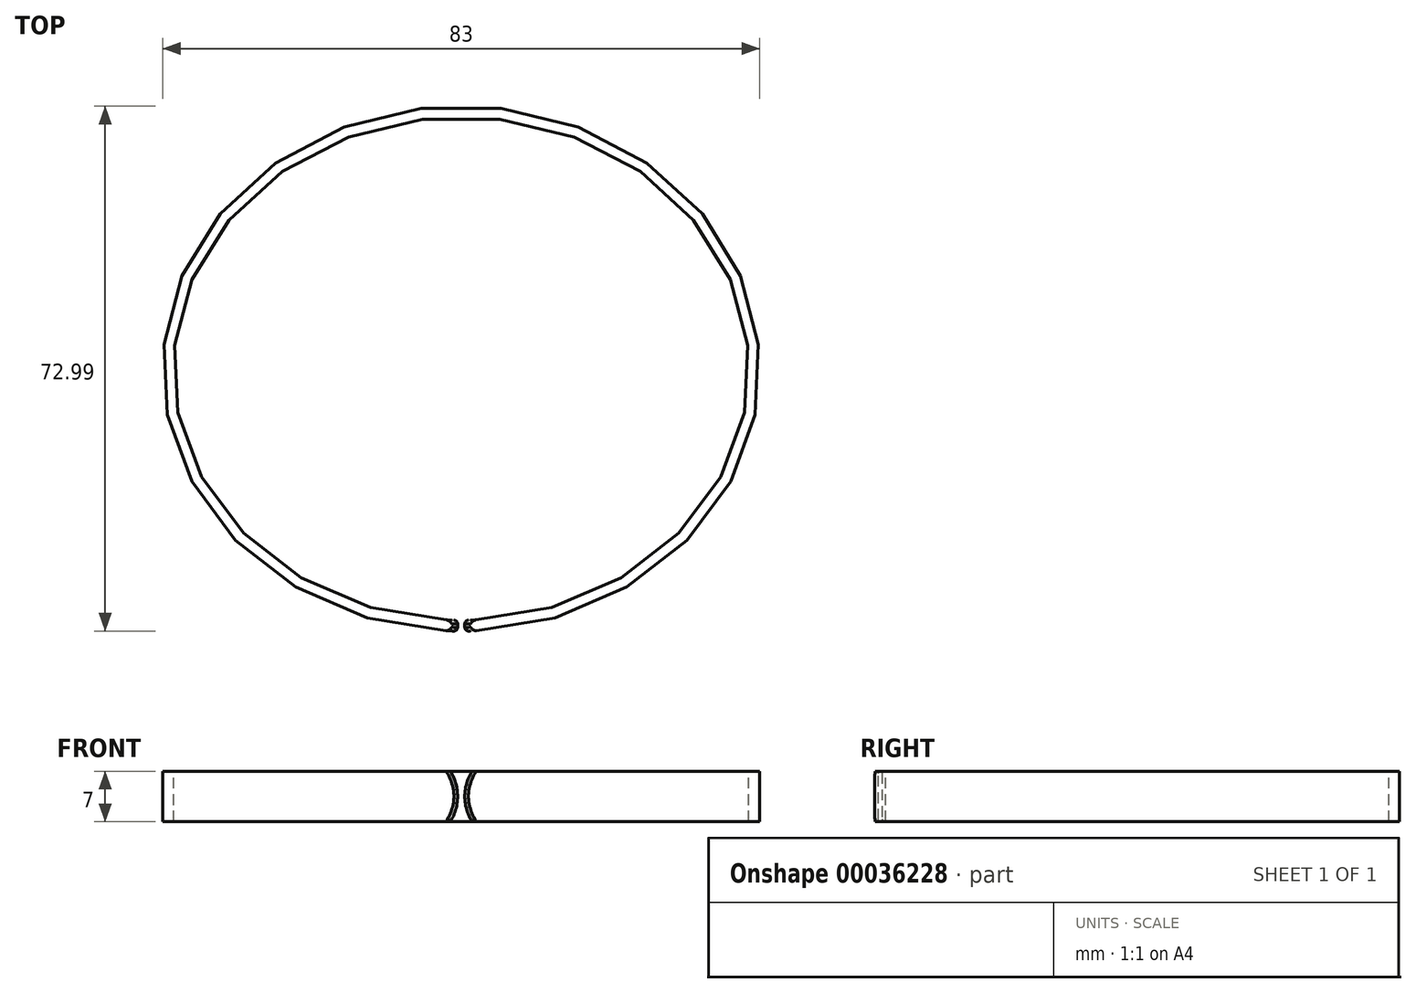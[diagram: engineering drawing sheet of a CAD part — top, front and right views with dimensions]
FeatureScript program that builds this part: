
annotation { "Feature Type Name" : "Feature", "Feature Type Description" : "" }
export const myFeature = defineFeature(function(context is Context, id is Id, definition is map)
    precondition{}
    {
        {
            var Q0;
            Q0=qCreatedBy(makeId("Top.planeOp"),FACE);
            var sketch = newSketch(context, id + "F0", { "sketchPlane" : qUnion([Q0])});
            skEllipse(sketch, "E0", {"center": v(0, 0) * mm, "majorRadius": 40 * mm, "minorRadius": 35 * mm, "majorAxis": v(1, 0)});
            skEllipse(sketch, "E1", {"center": v(0, 0) * mm, "majorRadius": 41.5 * mm, "minorRadius": 36.5 * mm, "majorAxis": v(1, 0)});
            skLineSegment(sketch, "E2", {"start": v(40, 0) * mm, "end": v(41.5, 0) * mm, "construction": true});
            skLineSegment(sketch, "E3", {"start": v(0, 35) * mm, "end": v(0, 36.5) * mm, "construction": true});
            skSolve(sketch);
        }
        {
            var Q0;
            Q0=qSketchRegion(id+"F0",true);
            extrude(context, id + "F1", {"entities" : qUnion([Q0]), "depth" : 7 * mm});
        }
        {
            var Q0;
            Q0=qCreatedBy(makeId("Front.planeOp"),FACE);
            var sketch = newSketch(context, id + "F2", { "sketchPlane" : qUnion([Q0])});
            skLineSegment(sketch, "E4", {"start": v(0, 0) * mm, "end": v(0, 7) * mm, "construction": true});
            skLineSegment(sketch, "E5", {"start": v(-0.5, 3.5) * mm, "end": v(0.5, 3.5) * mm, "construction": true});
            skPoint(sketch, "E5.startSnap0", {"position": v(0, 3.5) * mm});
            skLineSegment(sketch, "E6", {"start": v(-1.5, 7) * mm, "end": v(1.5, 7) * mm});
            skLineSegment(sketch, "E7", {"start": v(-1.5, 0) * mm, "end": v(1.5, 0) * mm});
            skArc(sketch, "E8", {"start": v(-1.5, 0) * mm, "mid": v(-0.5, 3.5) * mm, "end": v(-1.5, 7) * mm});
            skArc(sketch, "E9", {"start": v(1.5, 7) * mm, "mid": v(0.5, 3.5) * mm, "end": v(1.5, 0) * mm});
            skSolve(sketch);
        }
        {
            var Q0;
            Q0=makeQuery(id+"F2.imprint","IMPRINT",FACE,{"disambiguationData":[TD([[makeQuery(id+"F2.imprint","IMPRINT",EDGE,{"derivedFrom":sQuery(id+"F2.wireOp",EDGE,"E6")}),-1.0]])]});
            var Q1;
            Q1 = qConstructionFilter(qBodyType(qCreatedBy(id + "F2" ,EDGE), BodyType.WIRE), ConstructionObject.NO);
            extrude(context, id + "F3", {"entities" : qUnion([Q0]), "operationType" : NewBodyOperationType.REMOVE, "surfaceEntities" : qUnion([Q1]), "endBound" : BoundingType.THROUGH_ALL, "depth" : 25 * mm});
        }
        {
            var Q0;
            Q0=makeQuery(id+"F3.boolean.opBoolean","COPY",FACE,{"derivedFrom":makeQuery(id+"F3.opExtrude","SWEPT_FACE",FACE,{"disambiguationData":[OSD([sQuery(id+"F2.wireOp",EDGE,"E8")])]})});
            var Q1;
            Q1=makeQuery(id+"F3.boolean.opBoolean","COPY",FACE,{"derivedFrom":makeQuery(id+"F3.opExtrude","SWEPT_FACE",FACE,{"disambiguationData":[OSD([sQuery(id+"F2.wireOp",EDGE,"E9")])]})});
            fillet(context, id + "F4", {"entities" : qUnion([Q0, Q1]), "radius" : .5 * mm, "tangentPropagation" : true, "allowEdgeOverflow" : false});
        }
    });
